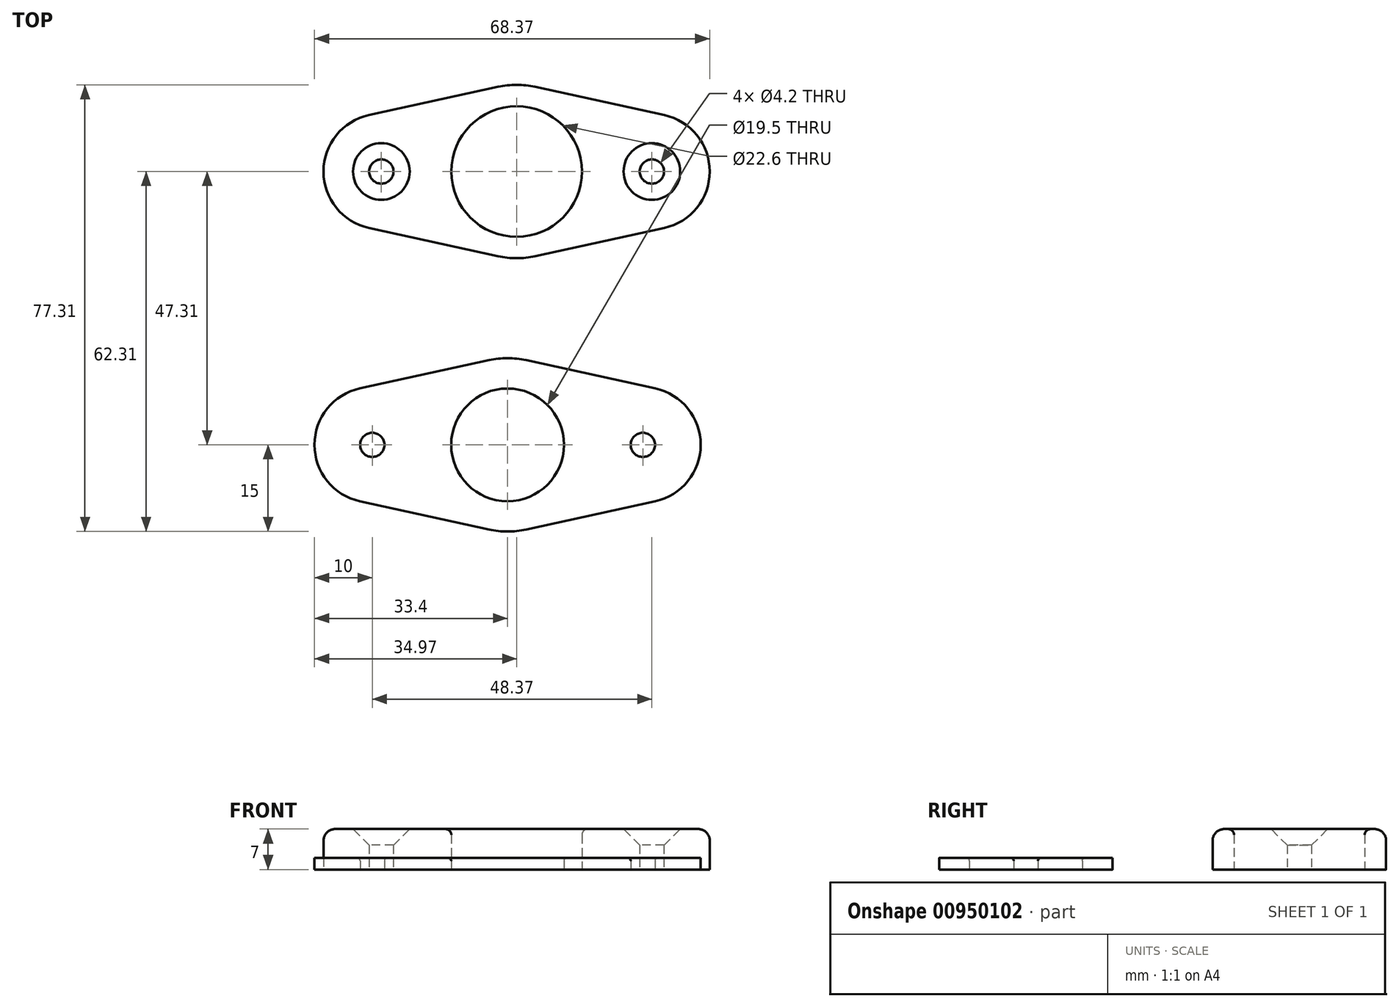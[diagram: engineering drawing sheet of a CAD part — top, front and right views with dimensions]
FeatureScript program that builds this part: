
annotation { "Feature Type Name" : "Feature", "Feature Type Description" : "" }
export const myFeature = defineFeature(function(context is Context, id is Id, definition is map)
    precondition{}
    {
        {
            var Q0;
            Q0=qCreatedBy(makeId("Top.planeOp"),FACE);
            var sketch = newSketch(context, id + "F0", { "sketchPlane" : qUnion([Q0])});
            skCircle(sketch, "E0", {"center": v(0, 0) * mm, "radius": 11.3 * mm});
            skCircle(sketch, "E1", {"center": v(-23.4, 0) * mm, "radius": 2.1 * mm});
            skCircle(sketch, "E2", {"center": v(23.4, 0) * mm, "radius": 2.1 * mm});
            skArc(sketch, "E3", {"start": v(-3.2, -14.65) * mm, "mid": v(0, -15) * mm, "end": v(3.2, -14.65) * mm});
            skLineSegment(sketch, "E4", {"start": v(25.54, -9.77) * mm, "end": v(3.2, -14.65) * mm});
            skLineSegment(sketch, "E5", {"start": v(3.2, 14.65) * mm, "end": v(25.54, 9.77) * mm});
            skLineSegment(sketch, "E6", {"start": v(-25.54, -9.77) * mm, "end": v(-3.2, -14.65) * mm});
            skLineSegment(sketch, "E7", {"start": v(-25.54, 9.77) * mm, "end": v(-3.2, 14.65) * mm});
            skArc(sketch, "E8.trimOffspring", {"start": v(25.54, -9.77) * mm, "mid": v(33.4, 0) * mm, "end": v(25.54, 9.77) * mm});
            skArc(sketch, "E9.trimOffspring", {"start": v(-25.54, 9.77) * mm, "mid": v(-33.4, 0) * mm, "end": v(-25.54, -9.77) * mm});
            skArc(sketch, "E10.trimOffspring", {"start": v(3.2, 14.65) * mm, "mid": v(0, 15) * mm, "end": v(-3.2, 14.65) * mm});
            skPoint(sketch, "E11.end.orphan", {"position": v(0, -15.35) * mm});
            skSolve(sketch);
        }
        {
            var Q0;
            Q0=makeQuery(id+"F0.imprint","IMPRINT",FACE,{"disambiguationData":[TD([[makeQuery(id+"F0.imprint","IMPRINT",EDGE,{"derivedFrom":sQuery(id+"F0.wireOp",EDGE,"E0")}),-1.0]])]});
            extrude(context, id + "F1", {"entities" : qUnion([Q0]), "depth" : 7 * mm, "offsetDistance" : 25 * mm});
        }
        {
            var Q0;
            Q0=makeQuery(id+"F1.opExtrude","CAP_EDGE",EDGE,{"disambiguationData":[OSD([sQuery(id+"F0.wireOp",EDGE,"E0")])],"isStart":false});
            fillet(context, id + "F2", {"entities" : qUnion([Q0]), "radius" : 1 * mm, "tangentPropagation" : true, "allowEdgeOverflow" : false});
        }
        {
            var Q0;
            Q0=makeQuery(id+"F1.opExtrude","CAP_EDGE",EDGE,{"disambiguationData":[OSD([sQuery(id+"F0.wireOp",EDGE,"E9.trimOffspring")])],"isStart":false});
            var Q1;
            Q1=makeQuery(id+"F1.opExtrude","CAP_EDGE",EDGE,{"disambiguationData":[OSD([sQuery(id+"F0.wireOp",EDGE,"E6")])],"isStart":false});
            var Q2;
            Q2=makeQuery(id+"F1.opExtrude","CAP_EDGE",EDGE,{"disambiguationData":[OSD([sQuery(id+"F0.wireOp",EDGE,"E7")])],"isStart":false});
            var Q3;
            Q3=makeQuery(id+"F1.opExtrude","CAP_EDGE",EDGE,{"disambiguationData":[OSD([sQuery(id+"F0.wireOp",EDGE,"E3")])],"isStart":false});
            var Q4;
            Q4=makeQuery(id+"F1.opExtrude","CAP_EDGE",EDGE,{"disambiguationData":[OSD([sQuery(id+"F0.wireOp",EDGE,"E4")])],"isStart":false});
            var Q5;
            Q5=makeQuery(id+"F1.opExtrude","CAP_EDGE",EDGE,{"disambiguationData":[OSD([sQuery(id+"F0.wireOp",EDGE,"E8.trimOffspring")])],"isStart":false});
            var Q6;
            Q6=makeQuery(id+"F1.opExtrude","CAP_EDGE",EDGE,{"disambiguationData":[OSD([sQuery(id+"F0.wireOp",EDGE,"E5")])],"isStart":false});
            var Q7;
            Q7=makeQuery(id+"F1.opExtrude","CAP_EDGE",EDGE,{"disambiguationData":[OSD([sQuery(id+"F0.wireOp",EDGE,"E10.trimOffspring")])],"isStart":false});
            fillet(context, id + "F3", {"entities" : qUnion([Q0, Q1, Q2, Q3, Q4, Q5, Q6, Q7]), "radius" : 2 * mm, "tangentPropagation" : true, "allowEdgeOverflow" : false});
        }
        {
            var Q0;
            Q0=makeQuery(id+"F1.opExtrude","CAP_EDGE",EDGE,{"disambiguationData":[OSD([sQuery(id+"F0.wireOp",EDGE,"E1")])],"isStart":false});
            var Q1;
            Q1=makeQuery(id+"F1.opExtrude","CAP_EDGE",EDGE,{"disambiguationData":[OSD([sQuery(id+"F0.wireOp",EDGE,"E2")])],"isStart":false});
            chamfer(context, id + "F4", {"entities" : qUnion([Q0, Q1]), "width" : 2.8 * mm, "tangentPropagation" : true});
        }
        {
            var Q0;
            Q0=qCreatedBy(makeId("Top.planeOp"),FACE);
            var sketch = newSketch(context, id + "F5", { "sketchPlane" : qUnion([Q0])});
            skCircle(sketch, "E12", {"center": v(-1.57, -47.3) * mm, "radius": 9.75 * mm});
            skCircle(sketch, "E13", {"center": v(-24.97, -47.3) * mm, "radius": 2.1 * mm});
            skCircle(sketch, "E14", {"center": v(21.83, -47.3) * mm, "radius": 2.1 * mm});
            skArc(sketch, "E15", {"start": v(-4.77, -61.96) * mm, "mid": v(-1.57, -62.3) * mm, "end": v(1.64, -61.96) * mm});
            skLineSegment(sketch, "E16", {"start": v(23.97, -57.08) * mm, "end": v(1.64, -61.96) * mm});
            skLineSegment(sketch, "E17", {"start": v(1.64, -32.66) * mm, "end": v(23.97, -37.54) * mm});
            skLineSegment(sketch, "E18", {"start": v(-27.1, -57.08) * mm, "end": v(-4.77, -61.96) * mm});
            skLineSegment(sketch, "E19", {"start": v(-27.1, -37.54) * mm, "end": v(-4.77, -32.66) * mm});
            skArc(sketch, "E20.trimOffspring", {"start": v(23.97, -57.08) * mm, "mid": v(31.83, -47.3) * mm, "end": v(23.97, -37.54) * mm});
            skArc(sketch, "E21.trimOffspring", {"start": v(-27.1, -37.54) * mm, "mid": v(-34.97, -47.3) * mm, "end": v(-27.1, -57.08) * mm});
            skArc(sketch, "E22.trimOffspring", {"start": v(1.64, -32.66) * mm, "mid": v(-1.57, -32.3) * mm, "end": v(-4.77, -32.66) * mm});
            skPoint(sketch, "E23.end.orphan", {"position": v(-1.57, -62.66) * mm});
            skSolve(sketch);
        }
        {
            var Q0;
            Q0 = qSketchRegion(id + "F5", true);
            extrude(context, id + "F6", {"entities" : qUnion([Q0]), "depth" : 2 * mm, "offsetDistance" : 25 * mm});
        }
        {
            var Q0;
            Q0=makeQuery(id+"F6.opExtrude","CAP_EDGE",EDGE,{"disambiguationData":[OSD([sQuery(id+"F5.wireOp",EDGE,"E13")])],"isStart":false});
            var Q1;
            Q1=makeQuery(id+"F6.opExtrude","CAP_EDGE",EDGE,{"disambiguationData":[OSD([sQuery(id+"F5.wireOp",EDGE,"E12")])],"isStart":false});
            var Q2;
            Q2=makeQuery(id+"F6.opExtrude","CAP_EDGE",EDGE,{"disambiguationData":[OSD([sQuery(id+"F5.wireOp",EDGE,"E14")])],"isStart":false});
            fillet(context, id + "F7", {"entities" : qUnion([Q0, Q1, Q2]), "radius" : .5 * mm, "tangentPropagation" : true, "allowEdgeOverflow" : false});
        }
    });
